# Revit family: Midmark - Fold-Up Lift Table
name_source: partatom
category: Specialty Equipment
revit_build: Autodesk Revit 2017 (Build: 20190507_1515(x64)
units: mm (PartAtom-declared; Revit-internal decimal feet)

## family parameters
Cut with Voids When Loaded = No
Host = Face
Part Type = Normal
Room Calculation Point = No
Round Connector Dimension = Use Diameter
Shared = No

## types (4) — shared parameters
Cleats Material = Stainless Steel, Polished
Default Elevation = 3' - 0"
Depth = 3' - 8"
Exam Table Material = Stainless Steel, Polished
Foot Control Material = Rubber, Black
Height = 6' - 8"
Lift Column Material = Stainless Steel, Polished
Lift Column Stand Material = Stainless Steel, Polished
Lift Column Stand Width = 2' - 10"
Manufacturer = MIDMARK
Plate Height = 1' - 4"
Plate Width = 1' - 10 3/4"
Plate thickness = 0' - 0 1/2"
Scale Display Material = Plastic, Opaque White
Table Back Support Plate Material = Stainless Steel, Polished
Table Back Support Rails Material = Stainless Steel, Polished
Table Frame Material = Steel, Paint Finish, Black, Matte
Table thickness = 0' - 1 7/16"
Width = 1' - 10"

## per-type parameters (varying)
| type | Foot Control | Model | Scale | Type Comments |
| Stainless Steel Top w/ Hand Control | No | 101-3310-10 | Yes | Electric Fold-up Lift Table, 44"L x 22"W Stainless Steel Top with Hand Control. |
| Stainless Steel Top w/ Foot Control | Yes | 101-5640-37 | No | Electric Fold-up Lift Table, 44"L x 22"W Stainless Steel Top with Foot Control |
| Stainless Steel Top w/ Hand Control & Scale | No | 101-3310-10 | Yes | Electric Fold-up Lift Table, 44"L x 22"W Stainless Steel Top with Hand Control and Built-in Scale |
| Stainless Steel Top w/ Foot Control & Scale | Yes | 101-3310-21 | Yes | Electric Fold-up Lift Table, 44"L x 22"W Stainless Steel Top with Foot Control and Built-in Scale |

## geometry (parser evidence)
native form markers: Sweep x2
no freeform markers — native parametric forms only
